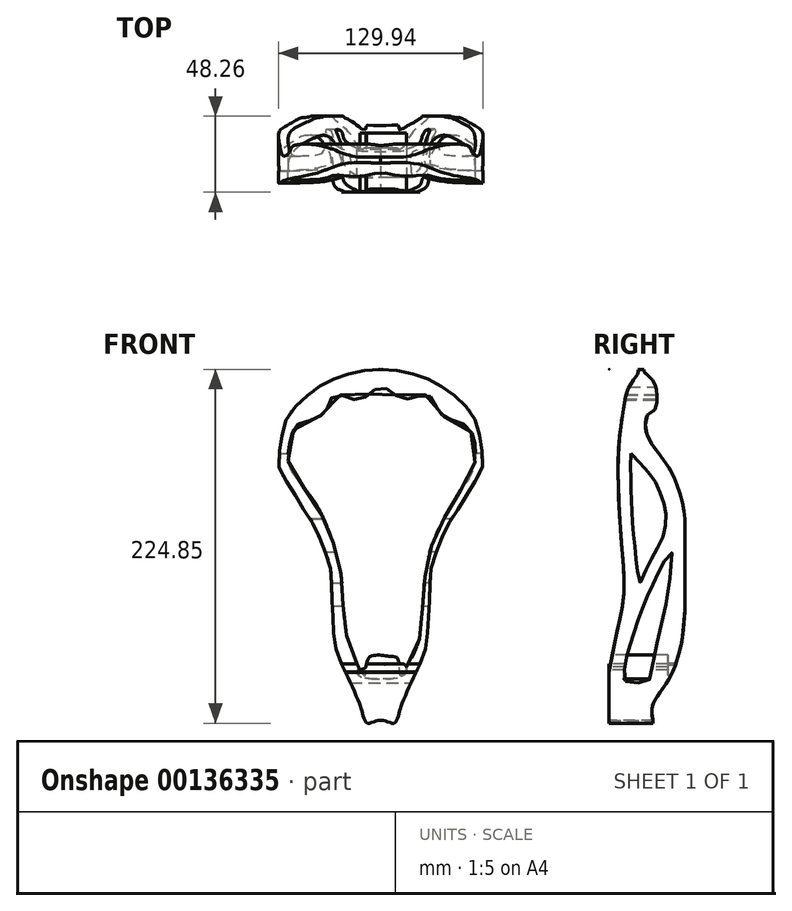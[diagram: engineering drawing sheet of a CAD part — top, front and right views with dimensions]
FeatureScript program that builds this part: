
annotation { "Feature Type Name" : "Feature", "Feature Type Description" : "" }
export const myFeature = defineFeature(function(context is Context, id is Id, definition is map)
    precondition{}
    {
        {
            var Q0;
            Q0=qCreatedBy(makeId("Front.planeOp"),FACE);
            var sketch = newSketch(context, id + "F0", { "sketchPlane" : qUnion([Q0])});
            skLineSegment(sketch, "E0", {"start": v(0, -72.83) * mm, "end": v(0, 150.24) * mm});
            skFitSpline(sketch, "E1", {"points": [v(0, 150.24) * mm, v(-1.48, 150.24) * mm, v(-4.3, 149.98) * mm, v(-9.4, 149.6) * mm, v(-12.84, 149.07) * mm, v(-16.02, 148.38) * mm, v(-20, 147.46) * mm, v(-25.8, 145.73) * mm, v(-31.7, 143.15) * mm, v(-37.82, 139.93) * mm, v(-51.56, 129.32) * mm, v(-60.43, 117.15) * mm, v(-64.43, 97.23) * mm, v(-64.26, 86.62) * mm, v(-56.78, 74.44) * mm, v(-49.65, 62.1) * mm, v(-45.82, 57.27) * mm, v(-39.73, 45.1) * mm, v(-34.34, 31.7) * mm, v(-31.9, 23.35) * mm, v(-31.04, 8.22) * mm, v(-30.34, -6.4) * mm, v(-28.43, -27.02) * mm, v(-20.77, -45.63) * mm, v(-13.64, -61.98) * mm, v(-11.9, -67.02) * mm, v(-10.34, -72.06) * mm, v(-8.43, -74.5) * mm, v(-4.95, -73.8) * mm, v(-1.64, -72.76) * mm, v(0, -72.83) * mm], "startDerivative": vector(-100.07, 3.17) * mm, "endDerivative": vector(103.4, -15.38) * mm});
            skSolve(sketch);
        }
        {
            var Q0;
            Q0=makeQuery(id+"F0.imprint","IMPRINT",FACE,{"disambiguationData":[TD([[makeQuery(id+"F0.imprint","IMPRINT",EDGE,{"derivedFrom":sQuery(id+"F0.wireOp",EDGE,"E0")}),1.0]])]});
            extrude(context, id + "F1", {"entities" : qUnion([Q0]), "oppositeDirection" : true, "depth" : 48.26 * mm});
        }
        {
            var Q0;
            Q0=makeQuery(id+"F1.opExtrude","SWEPT_BODY",BODY,{"disambiguationData":[OSD([sQuery(id+"F0.wireOp",EDGE,"E0"),sQuery(id+"F0.wireOp",EDGE,"E1")])]});
            var Q1;
            Q1=qCreatedBy(makeId("Right.planeOp"),FACE);
            mirror(context, id + "F2", {"operationType" : NewBodyOperationType.ADD, "entities" : qUnion([Q0]), "mirrorPlane" : qUnion([Q1])});
        }
        {
            var Q0;
            Q0=qCreatedBy(makeId("Right.planeOp"),FACE);
            var sketch = newSketch(context, id + "F3", { "sketchPlane" : qUnion([Q0])});
            skFitSpline(sketch, "E2", {"points": [v(0, -42.42) * mm, v(5.3, -15.25) * mm, v(8.62, 0) * mm, v(9.61, 14.25) * mm, v(7.95, 40.43) * mm, v(6.3, 64.3) * mm, v(6.05, 74.12) * mm, v(5.88, 81.69) * mm, v(5.88, 93.93) * mm, v(6.31, 104) * mm, v(8.94, 124.32) * mm, v(13.96, 141.36) * mm, v(18.55, 150.1) * mm, v(0, 150.26) * mm, v(0, -36.86) * mm, v(0, -42.42) * mm]});
            skSolve(sketch);
        }
        {
            var Q0;
            Q0=qCreatedBy(makeId("Right.planeOp"),FACE);
            var sketch = newSketch(context, id + "F4", { "sketchPlane" : qUnion([Q0])});
            skFitSpline(sketch, "E3", {"points": [v(10.32, -47.88) * mm, v(24.23, -48.44) * mm, v(25.9, -46.5) * mm, v(30.62, -23.4) * mm, v(37.02, 5.8) * mm, v(39.25, 24.16) * mm, v(39.53, 34.17) * mm, v(32.3, 22.77) * mm, v(20.8, -2.5) * mm, v(16.03, -16.67) * mm, v(13.18, -25.3) * mm, v(10.15, -38.42) * mm, v(9.43, -46.35) * mm, v(10.32, -47.88) * mm]});
            skSolve(sketch);
        }
        {
            var Q0;
            Q0=qSketchRegion(id+"F4",true);
            extrude(context, id + "F5", {"entities" : qUnion([Q0]), "operationType" : NewBodyOperationType.REMOVE, "endBound" : BoundingType.SYMMETRIC, "oppositeDirection" : true, "depth" : 127 * mm});
        }
        {
            var Q0;
            Q0=qCreatedBy(makeId("Right.planeOp"),FACE);
            var sketch = newSketch(context, id + "F6", { "sketchPlane" : qUnion([Q0])});
            skFitSpline(sketch, "E4", {"points": [v(13.88, 96.8) * mm, v(13.72, 83.36) * mm, v(14.2, 67.88) * mm, v(15.62, 45.6) * mm, v(17.51, 27.12) * mm, v(19.25, 14.55) * mm, v(21.78, 19.3) * mm, v(28.89, 33.2) * mm, v(34.1, 43.3) * mm, v(36.16, 55) * mm, v(34.26, 67) * mm, v(27.78, 81.38) * mm, v(22.4, 87.86) * mm, v(16.09, 94.97) * mm, v(14.62, 96.3) * mm, v(13.88, 96.8) * mm]});
            skSolve(sketch);
        }
        {
            var Q0;
            Q0=qSketchRegion(id+"F6",true);
            extrude(context, id + "F7", {"entities" : qUnion([Q0]), "operationType" : NewBodyOperationType.REMOVE, "endBound" : BoundingType.SYMMETRIC, "depth" : 152.4 * mm});
        }
        {
            var Q0;
            Q0=qCreatedBy(makeId("Right.planeOp"),FACE);
            var sketch = newSketch(context, id + "F8", { "sketchPlane" : qUnion([Q0])});
            skFitSpline(sketch, "E5", {"points": [v(48.29, 55.32) * mm, v(47.36, 62.26) * mm, v(44.82, 71.9) * mm, v(39.67, 84.9) * mm, v(28.84, 100.6) * mm, v(23.15, 112.51) * mm, v(25.05, 121.72) * mm, v(28.57, 123.88) * mm, v(30.47, 134.44) * mm, v(26.4, 144.73) * mm, v(22.34, 150.42) * mm, v(48.6, 150.15) * mm, v(48.29, 55.32) * mm]});
            skSolve(sketch);
        }
        {
            var Q0;
            Q0=makeQuery(id+"F8.imprint","IMPRINT",FACE,{"disambiguationData":[TD([[makeQuery(id+"F8.imprint","IMPRINT",EDGE,{"derivedFrom":sQuery(id+"F8.wireOp",EDGE,"E5")}),-1.0]])]});
            extrude(context, id + "F9", {"entities" : qUnion([Q0]), "operationType" : NewBodyOperationType.REMOVE, "endBound" : BoundingType.SYMMETRIC, "depth" : 152.4 * mm});
        }
        {
            var Q0;
            Q0=qCreatedBy(makeId("Front.planeOp"),FACE);
            var sketch = newSketch(context, id + "F10", { "sketchPlane" : qUnion([Q0])});
            skFitSpline(sketch, "E6", {"points": [v(12.08, -44) * mm, v(14.73, -41.19) * mm, v(19.87, -32.9) * mm, v(25.01, -18.46) * mm, v(26.18, -4.7) * mm, v(27.2, 7.62) * mm, v(27.97, 18.2) * mm, v(31.56, 35.9) * mm, v(38.5, 52.33) * mm, v(48.5, 70.03) * mm, v(57.99, 84.9) * mm, v(60.1, 96.01) * mm, v(59.08, 106.28) * mm, v(54.2, 114.49) * mm, v(44.45, 118.34) * mm, v(39.32, 120.64) * mm, v(36.5, 124.24) * mm, v(31.37, 132.96) * mm, v(28.55, 134.24) * mm, v(21.88, 132.7) * mm, v(14.44, 131.42) * mm, v(7.77, 135.27) * mm, v(0, 138.86) * mm, v(-8.4, 133.73) * mm, v(-15.84, 130.9) * mm, v(-23.54, 133.22) * mm, v(-28.4, 133.99) * mm, v(-31.49, 131.93) * mm, v(-32.77, 127.83) * mm, v(-36.36, 122.44) * mm, v(-43.03, 118.34) * mm, v(-50.22, 116.54) * mm, v(-55.6, 111.4) * mm, v(-58.17, 101.66) * mm, v(-58.17, 89.6) * mm, v(-47.14, 72.92) * mm, v(-38.67, 60.35) * mm, v(-30.46, 40.6) * mm, v(-24.82, 15.97) * mm, v(-22.77, -13.54) * mm, v(-16.6, -32.78) * mm, v(-11.99, -42.79) * mm, v(-9.94, -44.07) * mm, v(-8.91, -36.89) * mm, v(-5.58, -36.89) * mm, v(-2.24, -37.14) * mm, v(5.97, -37.14) * mm, v(10.84, -36.63) * mm, v(12.08, -44) * mm]});
            skSolve(sketch);
        }
        {
            var Q0;
            Q0=makeQuery(id+"F10.imprint","IMPRINT",FACE,{"disambiguationData":[TD([[makeQuery(id+"F10.imprint","IMPRINT",EDGE,{"derivedFrom":sQuery(id+"F10.wireOp",EDGE,"E6")}),1.0]])]});
            extrude(context, id + "F11", {"entities" : qUnion([Q0]), "operationType" : NewBodyOperationType.REMOVE, "endBound" : BoundingType.SYMMETRIC, "depth" : 228.6 * mm});
        }
        {
            var Q0;
            Q0=qCreatedBy(makeId("Right.planeOp"),FACE);
            var sketch = newSketch(context, id + "F12", { "sketchPlane" : qUnion([Q0])});
            skFitSpline(sketch, "E7", {"points": [v(48.25, -0.25) * mm, v(48.37, -74.61) * mm, v(28, -74.61) * mm, v(28.06, -73.94) * mm, v(27.6, -70.58) * mm, v(27.19, -66.2) * mm, v(27.8, -62.78) * mm, v(31.96, -55.58) * mm, v(36.87, -48.65) * mm, v(40.5, -41.86) * mm, v(42.46, -37.02) * mm, v(45.28, -26.91) * mm, v(46.7, -19.31) * mm, v(47.97, -6.06) * mm, v(48.24, -2.3) * mm, v(48.25, -0.25) * mm]});
            skSolve(sketch);
        }
        {
            var Q0;
            Q0=qSketchRegion(id+"F12",true);
            extrude(context, id + "F13", {"entities" : qUnion([Q0]), "operationType" : NewBodyOperationType.REMOVE, "endBound" : BoundingType.SYMMETRIC, "depth" : 228.6 * mm});
        }
        {
            var Q0;
            Q0=qCreatedBy(makeId("Front.planeOp"),FACE);
            var sketch = newSketch(context, id + "F14", { "sketchPlane" : qUnion([Q0])});
            skFitSpline(sketch, "E8", {"points": [v(-10.04, -39.49) * mm, v(-7.93, -33.4) * mm, v(0, -31.3) * mm, v(6.09, -32.08) * mm, v(10.32, -32.88) * mm, v(11.9, -36.31) * mm, v(15.34, -37.37) * mm, v(15.08, -43.45) * mm, v(-4.76, -46.36) * mm, v(-13.48, -44.51) * mm, v(-15.33, -41.34) * mm, v(-10.04, -39.49) * mm]});
            skSolve(sketch);
        }
        {
            var Q0;
            Q0=makeQuery(id+"F14.imprint","IMPRINT",FACE,{"disambiguationData":[TD([[makeQuery(id+"F14.imprint","IMPRINT",EDGE,{"derivedFrom":sQuery(id+"F14.wireOp",EDGE,"E8")}),-1.0]])]});
            extrude(context, id + "F15", {"entities" : qUnion([Q0]), "operationType" : NewBodyOperationType.ADD, "oppositeDirection" : true, "depth" : 37.46 * mm});
        }
        {
            var Q0;
            Q0=makeQuery(id+"F3.imprint","IMPRINT",FACE,{"disambiguationData":[TD([[makeQuery(id+"F3.imprint","IMPRINT",EDGE,{"derivedFrom":sQuery(id+"F3.wireOp",EDGE,"E2")}),1.0]])]});
            extrude(context, id + "F16", {"entities" : qUnion([Q0]), "operationType" : NewBodyOperationType.REMOVE, "endBound" : BoundingType.SYMMETRIC, "depth" : 228.6 * mm});
        }
    });
